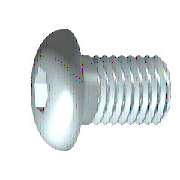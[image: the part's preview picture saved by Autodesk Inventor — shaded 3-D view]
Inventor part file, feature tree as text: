
AUTODESK INVENTOR PART (.ipt)
format: ipt  version: 2017 (Build 210142000, 142)  size: 198,656 bytes
history: native  units: mm (DEFAULTED — no unit token found)
features: sketch x2, extrude x1, plane x1, fillet x1
ambient origin geometry x7: Origin, YZ Plane, XY Plane, X Axis, Y Axis, Z Axis, Center Point
bodies: Solid1 (feature_tree), Body (feature_tree)
feature tree (5):
  extrude  "Slot"  Depth=1.8542mm
  plane  "Work Plane1"
  fillet  "Fillet2"  Radius=1.8542mm
  sketch  "Sketch1"  dims[d1=4.75976mm d2=1.59014mm d3=1.8542mm]
  sketch  "Sketch2"  dims[d4=1.1176mm d5=60.0deg d6=3.5052mm d7=3.5052mm d8=2.287693mm d9=6.6548mm d10=90.0deg d11=10.0mm d12=0.0mm d13=4.75976mm d14=0.0mm d15=0.486918mm d16=0.486918mm d17=1.6002mm d19=0.0mm d26=6.35mm d27=45.0deg d28=0.0mm d29=0.0mm d30=0.1mm]
